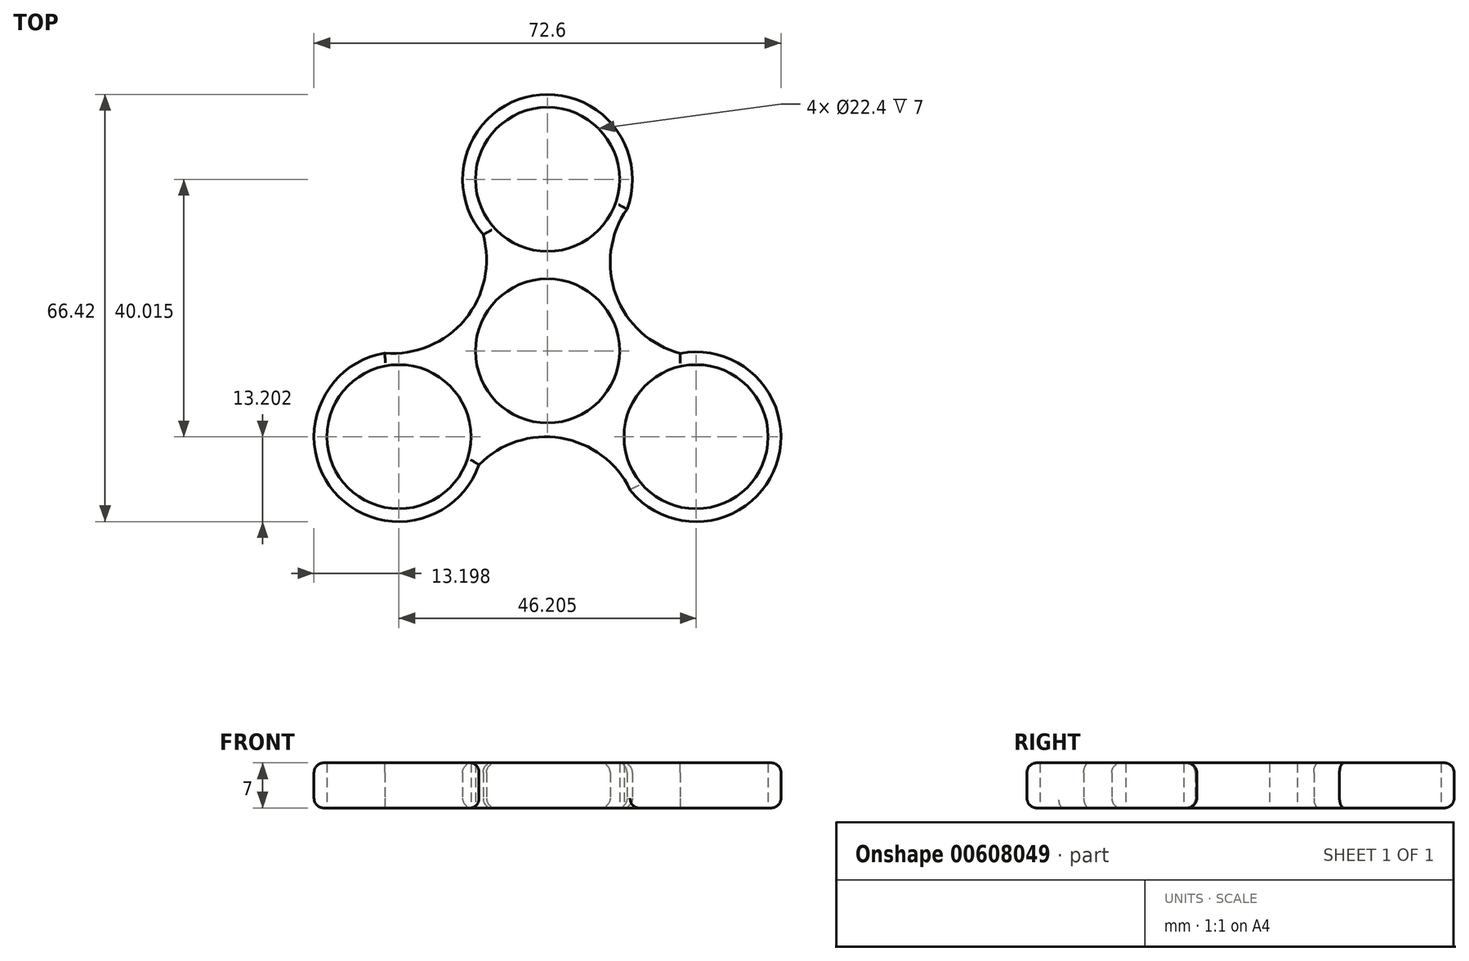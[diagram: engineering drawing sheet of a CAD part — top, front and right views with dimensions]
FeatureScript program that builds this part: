
annotation { "Feature Type Name" : "Feature", "Feature Type Description" : "" }
export const myFeature = defineFeature(function(context is Context, id is Id, definition is map)
    precondition{}
    {
        {
            var Q0;
            Q0=qCreatedBy(makeId("Top.planeOp"),FACE);
            var sketch = newSketch(context, id + "F0", { "sketchPlane" : qUnion([Q0])});
            skCircle(sketch, "E0", {"center": v(0, 0) * mm, "radius": 11.2 * mm});
            skCircle(sketch, "E1", {"center": v(0, 26.68) * mm, "radius": 11.2 * mm});
            skArc(sketch, "E2", {"start": v(10.73, 18.98) * mm, "mid": v(-0.58, 39.86) * mm, "end": v(-10, 18.07) * mm});
            skArc(sketch, "E3.1.0", {"start": v(-21.8, -0.2) * mm, "mid": v(-34.23, -20.43) * mm, "end": v(-10.65, -17.7) * mm});
            skCircle(sketch, "E3.1.1", {"center": v(-23.1, -13.34) * mm, "radius": 11.2 * mm});
            skArc(sketch, "E3.2.0", {"start": v(11.08, -18.78) * mm, "mid": v(34.81, -19.43) * mm, "end": v(20.66, -0.37) * mm});
            skCircle(sketch, "E3.2.1", {"center": v(23.1, -13.34) * mm, "radius": 11.2 * mm});
            skArc(sketch, "E4", {"start": v(12.36, 22.06) * mm, "mid": v(10.65, 8.68) * mm, "end": v(20.66, -0.37) * mm});
            skArc(sketch, "E5.1.0", {"start": v(-25.28, -0.32) * mm, "mid": v(-12.84, 4.88) * mm, "end": v(-10, 18.07) * mm});
            skArc(sketch, "E5.2.0", {"start": v(12.92, -21.74) * mm, "mid": v(2.2, -13.56) * mm, "end": v(-10.65, -17.7) * mm});
            skSolve(sketch);
        }
        {
            var Q0;
            Q0=makeQuery(id+"F0.imprint","IMPRINT",FACE,{"disambiguationData":[TD([[makeQuery(id+"F0.imprint","IMPRINT",EDGE,{"derivedFrom":sQuery(id+"F0.wireOp",EDGE,"E0")}),-1.0]])]});
            extrude(context, id + "F1", {"entities" : qUnion([Q0]), "depth" : 7 * mm, "offsetDistance" : 25 * mm});
        }
        {
            var Q0;
            Q0=makeQuery(id+"F1.opExtrude","CAP_EDGE",EDGE,{"disambiguationData":[OSD([sQuery(id+"F0.wireOp",EDGE,"E5.2.0")])],"isStart":false});
            var Q1;
            Q1=makeQuery(id+"F1.opExtrude","CAP_EDGE",EDGE,{"disambiguationData":[OSD([sQuery(id+"F0.wireOp",EDGE,"E5.2.0")])],"isStart":true});
            var Q2;
            Q2=makeQuery(id+"F1.opExtrude","CAP_EDGE",EDGE,{"disambiguationData":[OSD([sQuery(id+"F0.wireOp",EDGE,"E3.1.0")])],"isStart":false});
            var Q3;
            Q3=makeQuery(id+"F1.opExtrude","CAP_EDGE",EDGE,{"disambiguationData":[OSD([sQuery(id+"F0.wireOp",EDGE,"E5.1.0")])],"isStart":false});
            var Q4;
            Q4=makeQuery(id+"F1.opExtrude","CAP_EDGE",EDGE,{"disambiguationData":[OSD([sQuery(id+"F0.wireOp",EDGE,"E2")])],"isStart":false});
            var Q5;
            Q5=makeQuery(id+"F1.opExtrude","CAP_EDGE",EDGE,{"disambiguationData":[OSD([sQuery(id+"F0.wireOp",EDGE,"E3.2.0")])],"isStart":false});
            var Q6;
            Q6=makeQuery(id+"F1.opExtrude","CAP_EDGE",EDGE,{"disambiguationData":[OSD([sQuery(id+"F0.wireOp",EDGE,"E4")])],"isStart":false});
            fillet(context, id + "F2", {"entities" : qUnion([Q0, Q1, Q2, Q3, Q4, Q5, Q6]), "radius" : 1.5 * mm, "tangentPropagation" : true, "allowEdgeOverflow" : false});
        }
        {
            var Q0;
            Q0=makeQuery(id+"F1.opExtrude","CAP_EDGE",EDGE,{"disambiguationData":[OSD([sQuery(id+"F0.wireOp",EDGE,"E3.1.0")])],"isStart":true});
            var Q1;
            {var subQ0=sQuery(id+"F0.wireOp",EDGE,"E5.2.0");Q1=makeQuery(id+"F2.opFillet","BLEND_EDGE",EDGE,{"blendedFrom":[makeQuery(id+"F1.opExtrude","CAP_EDGE",EDGE,{"disambiguationData":[OSD([subQ0])],"isStart":true}),makeQuery(id+"F1.opExtrude","CAP_FACE",FACE,{"disambiguationData":[OSD([sQuery(id+"F0.wireOp",EDGE,"E0"),sQuery(id+"F0.wireOp",EDGE,"E1"),sQuery(id+"F0.wireOp",EDGE,"E2"),sQuery(id+"F0.wireOp",EDGE,"E3.1.0"),sQuery(id+"F0.wireOp",EDGE,"E3.1.1"),sQuery(id+"F0.wireOp",EDGE,"E3.2.0"),sQuery(id+"F0.wireOp",EDGE,"E3.2.1"),sQuery(id+"F0.wireOp",EDGE,"E4"),sQuery(id+"F0.wireOp",EDGE,"E5.1.0"),subQ0])],"isStart":true})],"blendedInto":[makeQuery(id+"F1.opExtrude","CAP_FACE",FACE,{"disambiguationData":[OSD([sQuery(id+"F0.wireOp",EDGE,"E0"),sQuery(id+"F0.wireOp",EDGE,"E1"),sQuery(id+"F0.wireOp",EDGE,"E2"),sQuery(id+"F0.wireOp",EDGE,"E3.1.0"),sQuery(id+"F0.wireOp",EDGE,"E3.1.1"),sQuery(id+"F0.wireOp",EDGE,"E3.2.0"),sQuery(id+"F0.wireOp",EDGE,"E3.2.1"),sQuery(id+"F0.wireOp",EDGE,"E4"),sQuery(id+"F0.wireOp",EDGE,"E5.1.0"),subQ0])],"isStart":true})]});}
            var Q2;
            Q2=makeQuery(id+"F1.opExtrude","CAP_EDGE",EDGE,{"disambiguationData":[OSD([sQuery(id+"F0.wireOp",EDGE,"E3.2.0")])],"isStart":true});
            var Q3;
            Q3=makeQuery(id+"F1.opExtrude","CAP_EDGE",EDGE,{"disambiguationData":[OSD([sQuery(id+"F0.wireOp",EDGE,"E4")])],"isStart":true});
            var Q4;
            Q4=makeQuery(id+"F1.opExtrude","CAP_EDGE",EDGE,{"disambiguationData":[OSD([sQuery(id+"F0.wireOp",EDGE,"E5.1.0")])],"isStart":true});
            var Q5;
            Q5=makeQuery(id+"F1.opExtrude","CAP_EDGE",EDGE,{"disambiguationData":[OSD([sQuery(id+"F0.wireOp",EDGE,"E2")])],"isStart":true});
            fillet(context, id + "F3", {"entities" : qUnion([Q0, Q1, Q2, Q3, Q4, Q5]), "radius" : 1.5 * mm, "tangentPropagation" : true, "allowEdgeOverflow" : false});
        }
    });
